# Revit family: SANINDUSA_118880004_Agres_77x35AgresUndermountBasin77x35_V0
name_source: partatom
category: Plumbing Fixtures
units: mm (PartAtom-declared; Revit-internal decimal feet)

## family parameters
Cut with Voids When Loaded = No
Host = Face
Part Type = Normal
Room Calculation Point = No
Round Connector Dimension = Use Diameter
Shared = No

## types (1)
- SANINDUSA_118880004_Agres_77x35AgresUndermountBasin77x35_V0
    AssetType = Fixed
    Category = Pr_40_20_96_18: Counter top wash basins
    CodePerformance = EN 14688:2006 CL 25
    Color = white
    Constituents = With embellisher ring and Fixing kit included
    Default Elevation = 1219 mm
    Description = Waste water appliance for washing the upper parts of the body.
    DrainSize = 47 mm  [stored 0.154199 ft]
    Element Type = WASHHANDBASIN: Waste water appliance for washing the upper parts of the body.
    Features = "Washbasin mounted on underside of countertop. Compatible
with Fixing kit 45, included"
    Finish = gloss
    Installation Instructions = https://www.tec.sanindusa.pt
    InstallationDate = 1900-12-31T23:59:59
    Manufacturer = Sanindusa
    ManufacturerName = Sanindusa
    ManufacturerURL = www.tec.sanindusa.pt
    Material = vitreous china
    Model = 118880004
    ModelNumber = 118880004
    ModelReference = Agres
    Name = 77x35 Agres washbasin
    NominalDepth = 110 mm  [stored 0.360892 ft]
    NominalHeight = 155 mm  [stored 0.50853 ft]
    NominalLength = 765 mm  [stored 2.50984 ft]
    NominalWidth = 345 mm  [stored 1.13189 ft]
    Pre-defined type (IFC) = WASHHANDBASIN
    ProductInformation = https://www.tec.sanindusa.pt
    ProductionYear = 2007
    Shape = rectangular
    Size = 77x35
    SpilloverLevel = 73
    Type (IFC) = IfcSanitaryTerminalType
    URL = www.tec.sanindusa.pt
    Version = 1
    WarrantyDescription = https://www.tec.sanindusa.pt
    WarrantyDurationParts = 5
    WarrantyDurationUnit = year
    WashHandBasinMounting = other
    WashHandBasinType = handrinse
    Waste Connection = Yes
    Weight = 10.74 kg

note: [stored X ft] marks values corroborated as IEEE doubles in the binary element streams (Revit-internal decimal feet)

## geometry (parser evidence)
native form markers: Sweep x7
no freeform markers — native parametric forms only
